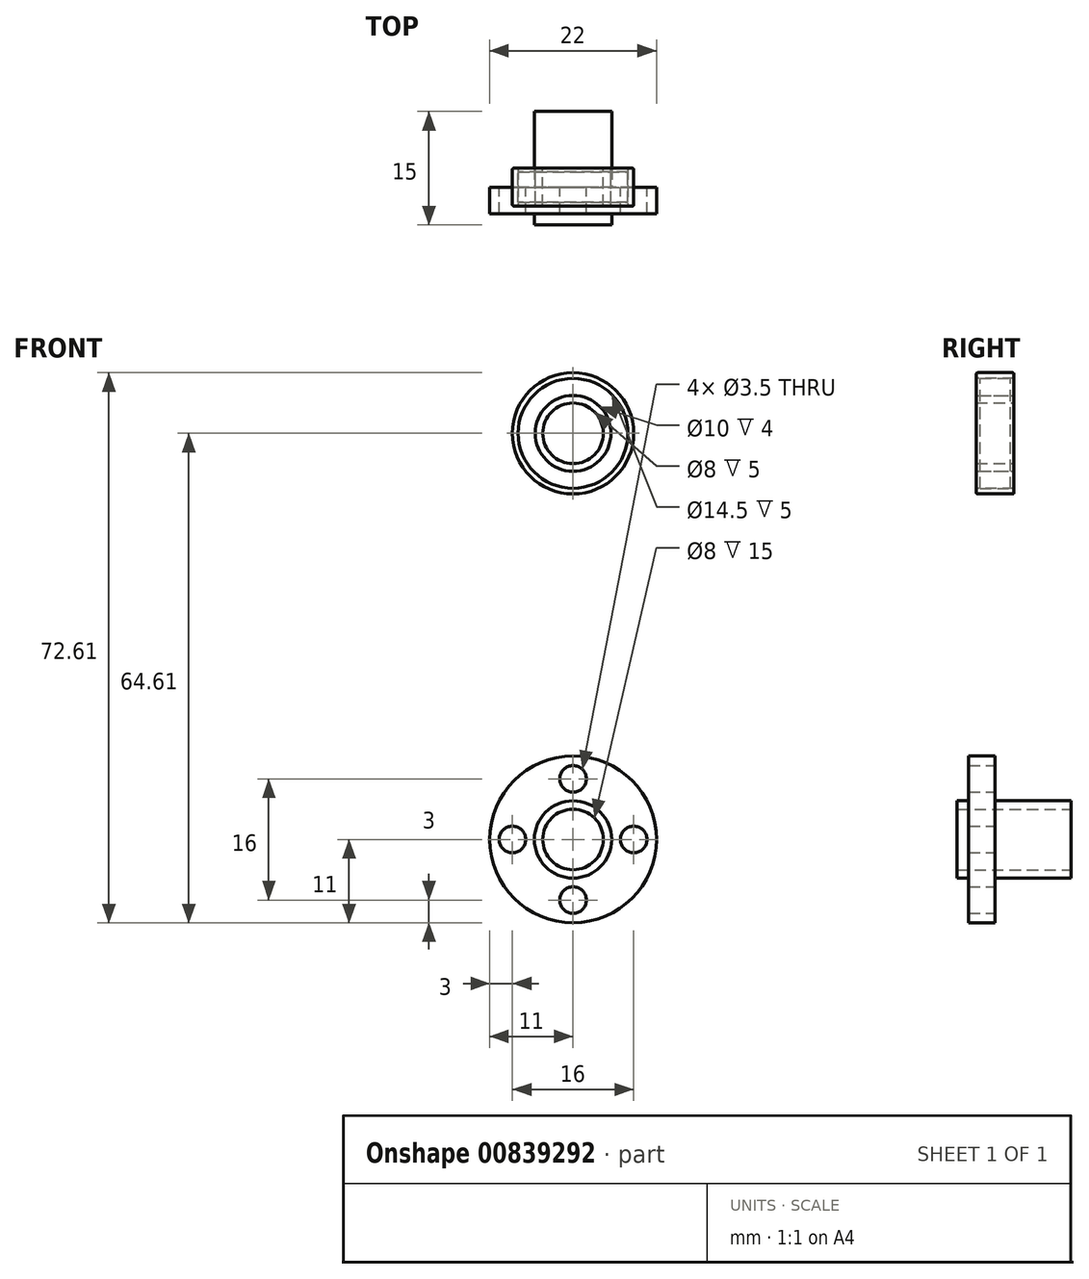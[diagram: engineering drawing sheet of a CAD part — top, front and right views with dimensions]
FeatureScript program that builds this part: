
annotation { "Feature Type Name" : "Feature", "Feature Type Description" : "" }
export const myFeature = defineFeature(function(context is Context, id is Id, definition is map)
    precondition{}
    {
        {
            var Q0;
            Q0=qCreatedBy(makeId("Front.planeOp"),FACE);
            var sketch = newSketch(context, id + "F0", { "sketchPlane" : qUnion([Q0])});
            skCircle(sketch, "E0", {"center": v(0, 0) * mm, "radius": 4 * mm});
            skCircle(sketch, "E1", {"center": v(0, 0) * mm, "radius": 8 * mm});
            skCircle(sketch, "E2", {"center": v(0, 0) * mm, "radius": 11 * mm});
            skCircle(sketch, "E3", {"center": v(0, 8) * mm, "radius": 1.75 * mm});
            skCircle(sketch, "E4.MirrorC", {"center": v(0, -8) * mm, "radius": 1.75 * mm});
            skCircle(sketch, "E5", {"center": v(8, 0) * mm, "radius": 1.75 * mm});
            skCircle(sketch, "E6.MirrorC", {"center": v(-8, 0) * mm, "radius": 1.75 * mm});
            skSolve(sketch);
        }
        {
            var Q0;
            Q0=makeQuery(id+"F0.imprint","IMPRINT",FACE,{"disambiguationData":[TD([[makeQuery(id+"F0.imprint","IMPRINT",EDGE,{"derivedFrom":sQuery(id+"F0.wireOp",EDGE,"E2")}),1.0]])]});
            var Q1;
            Q1=makeQuery(id+"F0.imprint","IMPRINT",FACE,{"disambiguationData":[TD([[makeQuery(id+"F0.imprint","IMPRINT",EDGE,{"derivedFrom":sQuery(id+"F0.wireOp",EDGE,"E0")}),-1.0]])]});
            extrude(context, id + "F1", {"entities" : qUnion([Q0, Q1]), "depth" : 3.5 * mm, "offsetDistance" : 25 * mm});
        }
        {
            var Q0;
            Q0=makeQuery(id+"F1.opExtrude","CAP_FACE",FACE,{"disambiguationData":[OSD([sQuery(id+"F0.wireOp",EDGE,"E0"),sQuery(id+"F0.wireOp",EDGE,"E2"),sQuery(id+"F0.wireOp",EDGE,"E3"),sQuery(id+"F0.wireOp",EDGE,"E4.MirrorC"),sQuery(id+"F0.wireOp",EDGE,"E5"),sQuery(id+"F0.wireOp",EDGE,"E6.MirrorC")])],"isStart":false});
            var sketch = newSketch(context, id + "F2", { "sketchPlane" : qUnion([Q0])});
            skCircle(sketch, "E7", {"center": v(0, 0) * mm, "radius": 5.1 * mm});
            skSolve(sketch);
        }
        {
            var Q0;
            Q0=makeQuery(id+"F2.imprint","IMPRINT",FACE,{"disambiguationData":[TD([[makeQuery(id+"F2.imprint","IMPRINT",EDGE,{"derivedFrom":sQuery(id+"F2.wireOp",EDGE,"E7")}),1.0]])]});
            extrude(context, id + "F3", {"entities" : qUnion([Q0]), "operationType" : NewBodyOperationType.ADD, "depth" : 1.5 * mm, "offsetDistance" : 25 * mm});
        }
        {
            var Q0;
            Q0=makeQuery(id+"F1.opExtrude","CAP_FACE",FACE,{"disambiguationData":[OSD([sQuery(id+"F0.wireOp",EDGE,"E0"),sQuery(id+"F0.wireOp",EDGE,"E2"),sQuery(id+"F0.wireOp",EDGE,"E3"),sQuery(id+"F0.wireOp",EDGE,"E4.MirrorC"),sQuery(id+"F0.wireOp",EDGE,"E5"),sQuery(id+"F0.wireOp",EDGE,"E6.MirrorC")])],"isStart":true});
            var sketch = newSketch(context, id + "F4", { "sketchPlane" : qUnion([Q0])});
            skCircle(sketch, "E8", {"center": v(0, 0) * mm, "radius": 5.1 * mm});
            skSolve(sketch);
        }
        {
            var Q0;
            Q0=makeQuery(id+"F4.imprint","IMPRINT",FACE,{"disambiguationData":[TD([[makeQuery(id+"F4.imprint","IMPRINT",EDGE,{"derivedFrom":sQuery(id+"F4.wireOp",EDGE,"E8")}),1.0]])]});
            extrude(context, id + "F5", {"entities" : qUnion([Q0]), "operationType" : NewBodyOperationType.ADD, "depth" : 10 * mm, "offsetDistance" : 25 * mm});
        }
        {
            var Q0;
            Q0=qCreatedBy(makeId("Front.planeOp"),FACE);
            var sketch = newSketch(context, id + "F6", { "sketchPlane" : qUnion([Q0])});
            skCircle(sketch, "E9", {"center": v(0, 53.61) * mm, "radius": 4 * mm});
            skCircle(sketch, "E10", {"center": v(0, 53.61) * mm, "radius": 5 * mm});
            skSolve(sketch);
        }
        {
            var Q0;
            Q0=makeQuery(id+"F6.imprint","IMPRINT",FACE,{"disambiguationData":[TD([[makeQuery(id+"F6.imprint","IMPRINT",EDGE,{"derivedFrom":sQuery(id+"F6.wireOp",EDGE,"E9")}),-1.0]])]});
            extrude(context, id + "F7", {"entities" : qUnion([Q0]), "endBound" : BoundingType.SYMMETRIC, "depth" : 5 * mm, "offsetDistance" : 25 * mm});
        }
        {
            var Q0;
            Q0=qCreatedBy(makeId("Front.planeOp"),FACE);
            var sketch = newSketch(context, id + "F8", { "sketchPlane" : qUnion([Q0])});
            skCircle(sketch, "E11", {"center": v(0, 53.61) * mm, "radius": 5 * mm});
            skCircle(sketch, "E12", {"center": v(0, 53.61) * mm, "radius": 7.25 * mm});
            skSolve(sketch);
        }
        {
            var Q0;
            Q0=makeQuery(id+"F8.imprint","IMPRINT",FACE,{"disambiguationData":[TD([[makeQuery(id+"F8.imprint","IMPRINT",EDGE,{"derivedFrom":sQuery(id+"F8.wireOp",EDGE,"E11")}),-1.0]])]});
            extrude(context, id + "F9", {"entities" : qUnion([Q0]), "endBound" : BoundingType.SYMMETRIC, "depth" : 4 * mm, "offsetDistance" : 25 * mm});
        }
        {
            var Q0;
            Q0=makeQuery(id+"F7.opExtrude","CAP_FACE",FACE,{"disambiguationData":[OSD([sQuery(id+"F6.wireOp",EDGE,"E9"),sQuery(id+"F6.wireOp",EDGE,"E10")])],"isStart":false});
            var sketch = newSketch(context, id + "F10", { "sketchPlane" : qUnion([Q0])});
            skCircle(sketch, "E13", {"center": v(0, 53.61) * mm, "radius": 7.25 * mm});
            skCircle(sketch, "E14", {"center": v(0, 53.61) * mm, "radius": 8 * mm});
            skSolve(sketch);
        }
        {
            var Q0;
            Q0=makeQuery(id+"F10.imprint","IMPRINT",FACE,{"disambiguationData":[TD([[makeQuery(id+"F10.imprint","IMPRINT",EDGE,{"derivedFrom":sQuery(id+"F10.wireOp",EDGE,"E13")}),-1.0]])]});
            extrude(context, id + "F11", {"entities" : qUnion([Q0]), "oppositeDirection" : true, "depth" : 5 * mm, "offsetDistance" : 25 * mm});
        }
        {
            var Q0;
            Q0=makeQuery(id+"F11.opExtrude","CAP_EDGE",EDGE,{"disambiguationData":[OSD([sQuery(id+"F10.wireOp",EDGE,"E14")])],"isStart":true});
            var Q1;
            Q1=makeQuery(id+"F11.opExtrude","CAP_EDGE",EDGE,{"disambiguationData":[OSD([sQuery(id+"F10.wireOp",EDGE,"E14")])],"isStart":false});
            fillet(context, id + "F12", {"entities" : qUnion([Q0, Q1]), "radius" : 0.2 * mm, "tangentPropagation" : true, "allowEdgeOverflow" : false});
        }
    });
